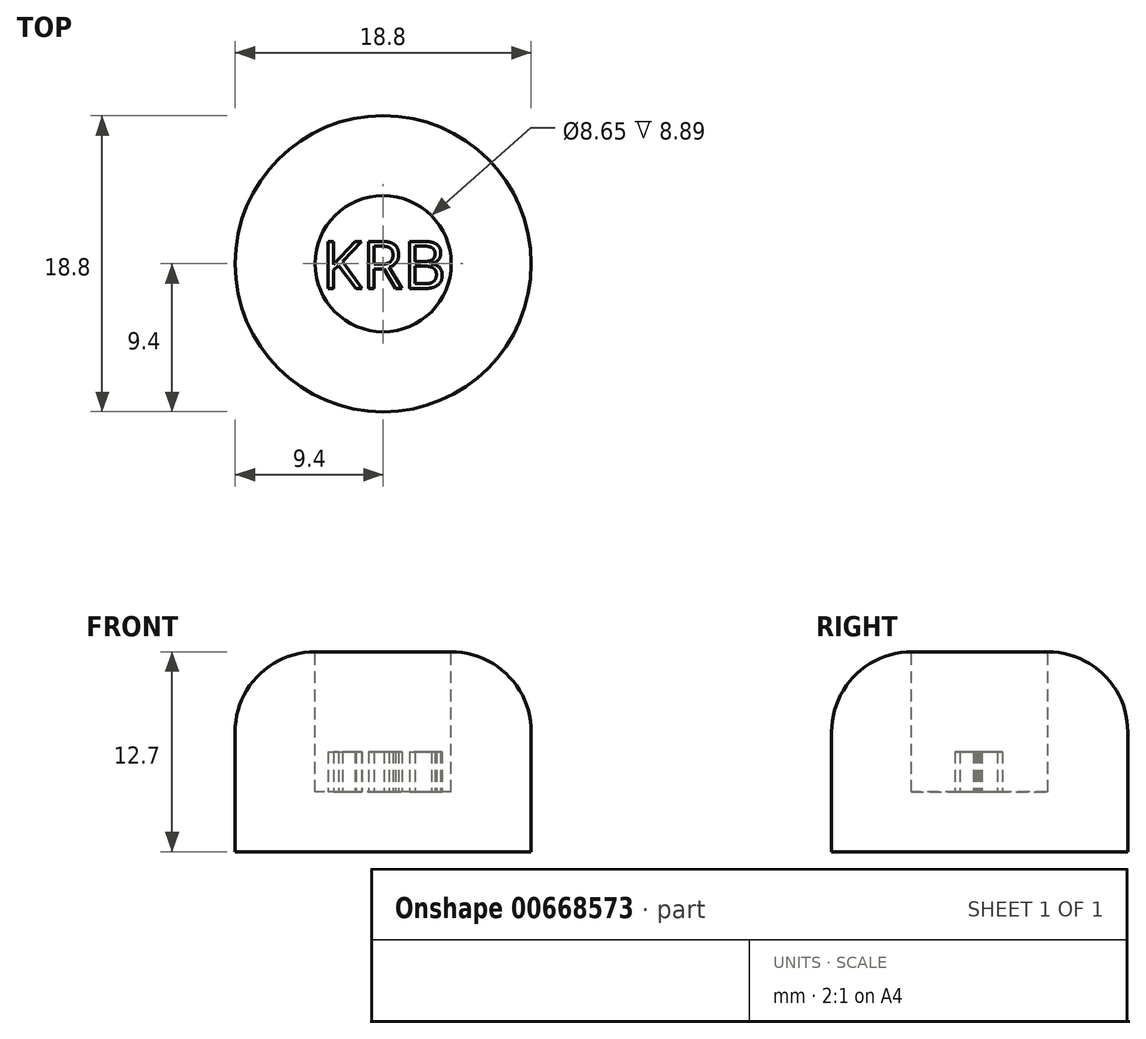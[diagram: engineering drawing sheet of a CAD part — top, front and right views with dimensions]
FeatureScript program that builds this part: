
annotation { "Feature Type Name" : "Feature", "Feature Type Description" : "" }
export const myFeature = defineFeature(function(context is Context, id is Id, definition is map)
    precondition{}
    {
        {
            var Q0;
            Q0=qCreatedBy(makeId("Top.planeOp"),FACE);
            var sketch = newSketch(context, id + "F0", { "sketchPlane" : qUnion([Q0])});
            skCircle(sketch, "E0", {"center": v(0, 0) * mm, "radius": 9.4 * mm});
            skSolve(sketch);
        }
        {
            var Q0;
            Q0=makeQuery(id+"F0.imprint","IMPRINT",FACE,{"disambiguationData":[TD([[makeQuery(id+"F0.imprint","IMPRINT",EDGE,{"derivedFrom":sQuery(id+"F0.wireOp",EDGE,"E0")}),1.0]])]});
            extrude(context, id + "F1", {"entities" : qUnion([Q0]), "depth" : 12.7 * mm, "offsetDistance" : 25.4 * mm});
        }
        {
            var Q0;
            Q0=qCreatedBy(makeId("Right.planeOp"),FACE);
            var sketch = newSketch(context, id + "F2", { "sketchPlane" : qUnion([Q0])});
            skLineSegment(sketch, "E1", {"start": v(0, 0) * mm, "end": v(0, -38.11) * mm});
            skSolve(sketch);
        }
        {
            var Q0;
            Q0=qCreatedBy(makeId("Right.planeOp"),FACE);
            var sketch = newSketch(context, id + "F3", { "sketchPlane" : qUnion([Q0])});
            skLineSegment(sketch, "E2", {"start": v(0, -38.58) * mm, "end": v(9.42, 0) * mm});
            skSolve(sketch);
        }
        {
            var Q0;
            Q0=sQuery(id+"F3.wireOp",EDGE,"E2");
            var Q1;
            Q1=sQuery(id+"F2.wireOp",EDGE,"E1");
            revolve(context, id + "F4", {"bodyType" : ToolBodyType.SURFACE, "surfaceEntities" : qUnion([Q0]), "axis" : qUnion([Q1]), "revolveType" : RevolveType.FULL});
        }
        {
            var Q0;
            Q0=makeQuery(id+"F1.opExtrude","CAP_FACE",FACE,{"disambiguationData":[OSD([sQuery(id+"F0.wireOp",EDGE,"E0")])],"isStart":false});
            fillet(context, id + "F5", {"entities" : qUnion([Q0]), "radius" : 5.08 * mm, "tangentPropagation" : true, "allowEdgeOverflow" : false});
        }
        {
            var Q0;
            Q0=makeQuery(id+"F1.opExtrude","CAP_FACE",FACE,{"disambiguationData":[OSD([sQuery(id+"F0.wireOp",EDGE,"E0")])],"isStart":false});
            extrude(context, id + "F6", {"entities" : qUnion([Q0]), "operationType" : NewBodyOperationType.REMOVE, "oppositeDirection" : true, "depth" : 8.9 * mm, "offsetDistance" : 25.4 * mm});
        }
        {
            var Q0;
            Q0=makeQuery(id+"F6.boolean.opBoolean","COPY",FACE,{"derivedFrom":makeQuery(id+"F6.opExtrude","CAP_FACE",FACE,{"disambiguationData":[OSD([sQuery(id+"F0.wireOp",EDGE,"E0")])],"isStart":false})});
            var sketch = newSketch(context, id + "F7", { "sketchPlane" : qUnion([Q0])});
            skText(sketch, "E3", { "text": "KRB", "fontName": "OpenSans-Regular.ttf"});
            const initialGuessF7  = {"E3": [-0.0039, -0.00157, 1, 0, 0.00302]};
            skSetInitialGuess(sketch, initialGuessF7);
            skSolve(sketch);
        }
        {
            var Q0;
            Q0 = qSketchRegion(id + "F7", true);
            extrude(context, id + "F8", {"entities" : qUnion([Q0]), "operationType" : NewBodyOperationType.ADD, "depth" : 2.54 * mm, "offsetDistance" : 25.4 * mm});
        }
    });
